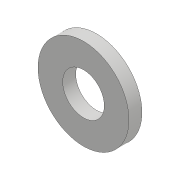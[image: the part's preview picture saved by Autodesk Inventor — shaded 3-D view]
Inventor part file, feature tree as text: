
AUTODESK INVENTOR PART (.ipt)
format: ipt  version: 2018 (Build 220112000, 112)  size: 81,920 bytes
history: native  units: mm
features: extrude x1, sketch x1
ambient origin geometry x8: Origin, YZ Plane, XZ Plane, XY Plane, X Axis, Y Axis, Z Axis, Center Point
bodies: Solid1 (feature_tree)
feature tree (2):
  extrude  "Extrusion1"  Depth=1.0mm
  sketch  "Sketch1"  dims[d0=7.0mm d1=3.2mm d2=1.0mm d3=0.0mm]
